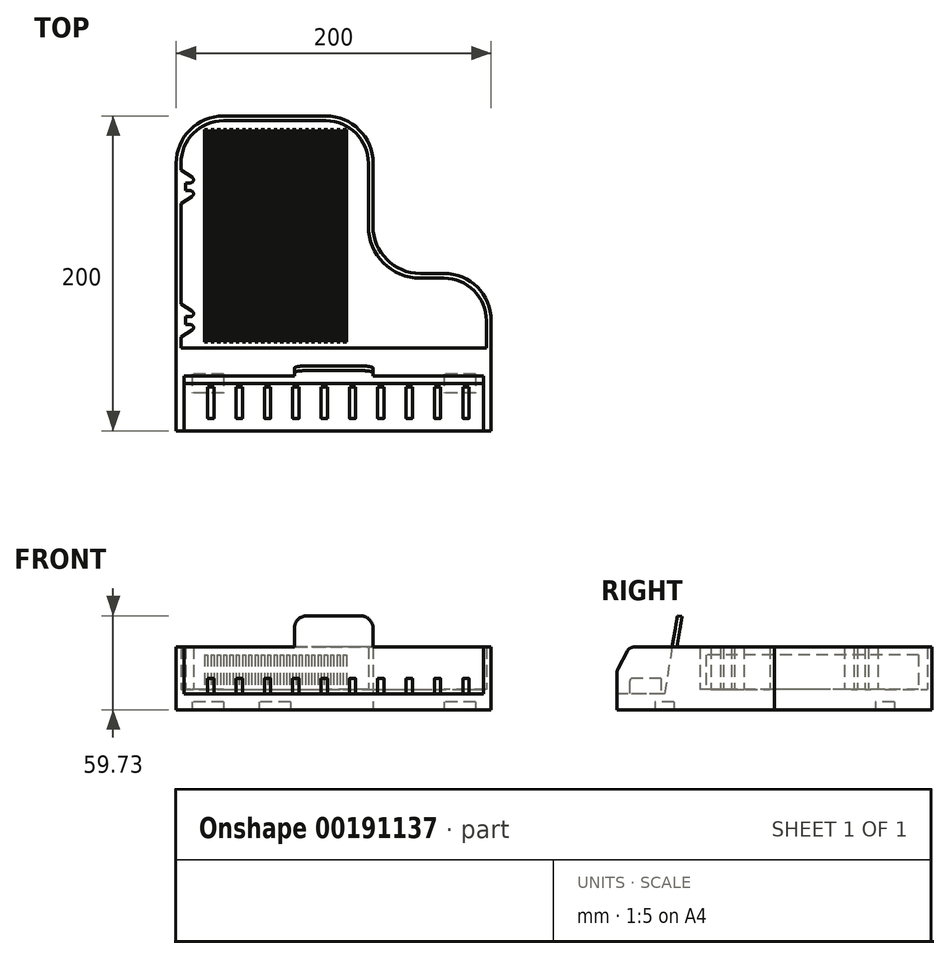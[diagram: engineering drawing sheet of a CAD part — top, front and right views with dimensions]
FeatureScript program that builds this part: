
annotation { "Feature Type Name" : "Feature", "Feature Type Description" : "" }
export const myFeature = defineFeature(function(context is Context, id is Id, definition is map)
    precondition{}
    {
        {
            var Q0;
            Q0=qCreatedBy(makeId("Top.planeOp"),FACE);
            var sketch = newSketch(context, id + "F0", { "sketchPlane" : qUnion([Q0])});
            skLineSegment(sketch, "E0.bottom", {"start": v(-100, 0) * mm, "end": v(100, 0) * mm});
            skLineSegment(sketch, "E0.top", {"start": v(-100, 200) * mm, "end": v(100, 200) * mm});
            skLineSegment(sketch, "E0.left", {"start": v(-100, 0) * mm, "end": v(-100, 200) * mm});
            skLineSegment(sketch, "E0.right", {"start": v(100, 0) * mm, "end": v(100, 200) * mm});
            skLineSegment(sketch, "E1.bottom", {"start": v(100, 200) * mm, "end": v(25, 200) * mm});
            skLineSegment(sketch, "E1.top", {"start": v(100, 100) * mm, "end": v(25, 100) * mm});
            skLineSegment(sketch, "E1.left", {"start": v(100, 200) * mm, "end": v(100, 100) * mm});
            skLineSegment(sketch, "E1.right", {"start": v(25, 200) * mm, "end": v(25, 100) * mm});
            skLineSegment(sketch, "E2", {"start": v(55, 209.14) * mm, "end": v(55, 81.97) * mm, "construction": true});
            skLineSegment(sketch, "E3", {"start": v(4.66, 130) * mm, "end": v(121.8, 130) * mm, "construction": true});
            skCircle(sketch, "E4", {"center": v(55, 130) * mm, "radius": 30 * mm});
            skLineSegment(sketch, "E5", {"start": v(70, 61.15) * mm, "end": v(70, 183.56) * mm, "construction": true});
            skLineSegment(sketch, "E6", {"start": v(-42.75, 70) * mm, "end": v(158.67, 70) * mm, "construction": true});
            skCircle(sketch, "E7", {"center": v(70, 70) * mm, "radius": 30 * mm});
            skPoint(sketch, "E7.centerSnap0", {"position": v(57.96, 70) * mm});
            skLineSegment(sketch, "E8", {"start": v(-5, 217.17) * mm, "end": v(-5, 99.03) * mm, "construction": true});
            skLineSegment(sketch, "E9", {"start": v(-141.82, 170) * mm, "end": v(13.69, 170) * mm, "construction": true});
            skLineSegment(sketch, "E10", {"start": v(-70, 225.7) * mm, "end": v(-70, 105.3) * mm, "construction": true});
            skCircle(sketch, "E11", {"center": v(-70, 170) * mm, "radius": 30 * mm});
            skCircle(sketch, "E12", {"center": v(-5, 170) * mm, "radius": 30 * mm});
            skSolve(sketch);
        }
        {
            var Q0;
            {var subQ0=sQuery(id+"F0.wireOp",EDGE,"E7");var subQ1=makeQuery(id+"F0.imprint","INTERSECT",VERTEX,{"derivedFrom":[sQuery(id+"F0.wireOp",EDGE,"E0.right"),subQ0]});Q0=makeQuery(id+"F0.imprint","IMPRINT",FACE,{"disambiguationData":[TD([[makeQuery(id+"F0.imprint","IMPRINT",EDGE,{"disambiguationData":[TD([[subQ1,-1.0]])],"derivedFrom":subQ0}),1.0]])]});}
            var Q1;
            {var subQ0=sQuery(id+"F0.wireOp",EDGE,"E11");var subQ1=makeQuery(id+"F0.imprint","INTERSECT",VERTEX,{"derivedFrom":[sQuery(id+"F0.wireOp",EDGE,"E0.top"),subQ0]});Q1=makeQuery(id+"F0.imprint","IMPRINT",FACE,{"disambiguationData":[TD([[makeQuery(id+"F0.imprint","IMPRINT",EDGE,{"disambiguationData":[TD([[subQ1,-1.0]])],"derivedFrom":subQ0}),1.0]])]});}
            var Q2;
            {var subQ0=sQuery(id+"F0.wireOp",EDGE,"E12");var subQ1=makeQuery(id+"F0.imprint","INTERSECT",VERTEX,{"derivedFrom":[sQuery(id+"F0.wireOp",EDGE,"E0.top"),subQ0]});Q2=makeQuery(id+"F0.imprint","IMPRINT",FACE,{"disambiguationData":[TD([[makeQuery(id+"F0.imprint","IMPRINT",EDGE,{"disambiguationData":[TD([[subQ1,1.0]])],"derivedFrom":subQ0}),1.0]])]});}
            var Q3;
            {var subQ17=sQuery(id+"F0.wireOp",EDGE,"E0.bottom");Q3=makeQuery(id+"F0.imprint","IMPRINT",FACE,{"disambiguationData":[TD([[makeQuery(id+"F0.imprint","IMPRINT",EDGE,{"derivedFrom":subQ17}),1.0]])]});}
            var Q4;
            {var subQ0=sQuery(id+"F0.wireOp",EDGE,"E1.right");var subQ1=sQuery(id+"F0.wireOp",EDGE,"E1.top");var subQ2=makeQuery(id+"F0.imprint","INTERSECT",VERTEX,{"derivedFrom":[subQ1,subQ0]});Q4=makeQuery(id+"F0.imprint","IMPRINT",FACE,{"disambiguationData":[TD([[makeQuery(id+"F0.imprint","IMPRINT",EDGE,{"disambiguationData":[TD([[subQ2,1.0]])],"derivedFrom":subQ1}),-1.0]])]});}
            extrude(context, id + "F1", {"entities" : qUnion([Q0, Q1, Q2, Q3, Q4]), "depth" : 40 * mm});
        }
        {
            var Q0;
            Q0=qCreatedBy(makeId("Top.planeOp"),FACE);
            cPlane(context, id + "F2", {"entities" : qUnion([Q0]), "cplaneType" : CPlaneType.OFFSET, "offset" : 5 * mm, "width" : 150 * mm, "height" : 150 * mm});
        }
        {
            var Q0;
            Q0=qCreatedBy(id+"F2.planeOp",FACE);
            var sketch = newSketch(context, id + "F3", { "sketchPlane" : qUnion([Q0])});
            skArc(sketch, "E13", {"start": v(-70, 197) * mm, "mid": v(-89.1, 189.1) * mm, "end": v(-97, 170) * mm});
            skArc(sketch, "E14", {"start": v(22, 170) * mm, "mid": v(14.1, 189.1) * mm, "end": v(-5, 197) * mm});
            skArc(sketch, "E15", {"start": v(22, 130) * mm, "mid": v(31.67, 106.67) * mm, "end": v(55, 97) * mm});
            skArc(sketch, "E16", {"start": v(97, 70) * mm, "mid": v(89.1, 89.1) * mm, "end": v(70, 97) * mm});
            skLineSegment(sketch, "E17", {"start": v(55, 97) * mm, "end": v(70, 97) * mm});
            skLineSegment(sketch, "E18", {"start": v(-70, 197) * mm, "end": v(-5, 197) * mm});
            skLineSegment(sketch, "E19", {"start": v(22, 170) * mm, "end": v(22, 130) * mm});
            skLineSegment(sketch, "E20", {"start": v(-131.7, 52.53) * mm, "end": v(133.85, 52.53) * mm, "construction": true});
            skLineSegment(sketch, "E21", {"start": v(97, 70) * mm, "end": v(97, 52.53) * mm});
            skLineSegment(sketch, "E22", {"start": v(-97, 170) * mm, "end": v(-97, 52.53) * mm});
            skLineSegment(sketch, "E23", {"start": v(-97, 52.53) * mm, "end": v(97, 52.53) * mm});
            skSolve(sketch);
        }
        {
            var Q0;
            {var subQ0=sQuery(id+"F3.wireOp",EDGE,"E13");var subQ1=makeQuery(id+"F3.imprint","INTERSECT",VERTEX,{"derivedFrom":[subQ0,sQuery(id+"F3.wireOp",EDGE,"E18")]});Q0=makeQuery(id+"F3.imprint","IMPRINT",FACE,{"disambiguationData":[TD([[makeQuery(id+"F3.imprint","IMPRINT",EDGE,{"disambiguationData":[TD([[subQ1,-1.0]])],"derivedFrom":subQ0}),1.0]])]});}
            var Q1;
            {var subQ0=sQuery(id+"F3.wireOp",EDGE,"E14");var subQ1=makeQuery(id+"F3.imprint","INTERSECT",VERTEX,{"derivedFrom":[subQ0,sQuery(id+"F3.wireOp",EDGE,"E18")]});Q1=makeQuery(id+"F3.imprint","IMPRINT",FACE,{"disambiguationData":[TD([[makeQuery(id+"F3.imprint","IMPRINT",EDGE,{"disambiguationData":[TD([[subQ1,1.0]])],"derivedFrom":subQ0}),1.0]])]});}
            var Q2;
            {var subQ0=sQuery(id+"F3.wireOp",EDGE,"E16");var subQ1=makeQuery(id+"F3.imprint","INTERSECT",VERTEX,{"derivedFrom":[subQ0,sQuery(id+"F3.wireOp",EDGE,"E17")]});Q2=makeQuery(id+"F3.imprint","IMPRINT",FACE,{"disambiguationData":[TD([[makeQuery(id+"F3.imprint","IMPRINT",EDGE,{"disambiguationData":[TD([[subQ1,1.0]])],"derivedFrom":subQ0}),1.0]])]});}
            var Q3;
            {var subQ0=sQuery(id+"F3.wireOp",EDGE,"E17");Q3=makeQuery(id+"F3.imprint","IMPRINT",FACE,{"disambiguationData":[TD([[makeQuery(id+"F3.imprint","IMPRINT",EDGE,{"derivedFrom":subQ0}),-1.0]])]});}
            extrude(context, id + "F4", {"entities" : qUnion([Q0, Q1, Q2, Q3]), "operationType" : NewBodyOperationType.REMOVE, "depth" : 35.7 * mm, "hasSecondDirection" : true, "secondDirectionOppositeDirection" : false, "secondDirectionDepth" : 8 * mm});
        }
        {
            var Q0;
            Q0=qCreatedBy(makeId("Right.planeOp"),FACE);
            var sketch = newSketch(context, id + "F5", { "sketchPlane" : qUnion([Q0])});
            skLineSegment(sketch, "E24", {"start": v(0, 40) * mm, "end": v(35, 40) * mm});
            skLineSegment(sketch, "E25", {"start": v(35, 40) * mm, "end": v(30, 10) * mm});
            skLineSegment(sketch, "E26", {"start": v(30, 10) * mm, "end": v(0, 10) * mm});
            skLineSegment(sketch, "E27", {"start": v(0, 10) * mm, "end": v(0, 40) * mm});
            skSolve(sketch);
        }
        {
            var Q0;
            Q0 = qSketchRegion(id + "F5", true);
            extrude(context, id + "F6", {"entities" : qUnion([Q0]), "operationType" : NewBodyOperationType.REMOVE, "endBound" : BoundingType.SYMMETRIC, "oppositeDirection" : true, "depth" : 190 * mm});
        }
        {
            var Q0;
            Q0=makeQuery(id+"F1.opExtrude","CAP_FACE",FACE,{"disambiguationData":[OSD([sQuery(id+"F0.wireOp",EDGE,"E0.bottom"),sQuery(id+"F0.wireOp",EDGE,"E0.top"),sQuery(id+"F0.wireOp",EDGE,"E0.left"),sQuery(id+"F0.wireOp",EDGE,"E0.right"),sQuery(id+"F0.wireOp",EDGE,"E1.top"),sQuery(id+"F0.wireOp",EDGE,"E1.right"),sQuery(id+"F0.wireOp",EDGE,"E4"),sQuery(id+"F0.wireOp",EDGE,"E7"),sQuery(id+"F0.wireOp",EDGE,"E11"),sQuery(id+"F0.wireOp",EDGE,"E12")])],"isStart":true});
            var sketch = newSketch(context, id + "F7", { "sketchPlane" : qUnion([Q0])});
            skLineSegment(sketch, "E28", {"start": v(91.06, -170) * mm, "end": v(-146.06, -170) * mm, "construction": true});
            skLineSegment(sketch, "E29", {"start": v(132.2, -30) * mm, "end": v(-157.53, -30) * mm, "construction": true});
            skLineSegment(sketch, "E30", {"start": v(80, -126.3) * mm, "end": v(80, 24.1) * mm, "construction": true});
            skLineSegment(sketch, "E31", {"start": v(-37.5, -226.49) * mm, "end": v(-37.5, 33.36) * mm, "construction": true});
            skLineSegment(sketch, "E32", {"start": v(-80, -225.96) * mm, "end": v(-80, 32.57) * mm, "construction": true});
            skLineSegment(sketch, "E33.bottom", {"start": v(90, -36) * mm, "end": v(70, -36) * mm});
            skLineSegment(sketch, "E33.top", {"start": v(90, -24) * mm, "end": v(70, -24) * mm});
            skLineSegment(sketch, "E33.left", {"start": v(90, -36) * mm, "end": v(90, -24) * mm});
            skLineSegment(sketch, "E33.right", {"start": v(70, -36) * mm, "end": v(70, -24) * mm});
            skLineSegment(sketch, "E34.bottom", {"start": v(-70, -36) * mm, "end": v(-90, -36) * mm});
            skLineSegment(sketch, "E34.top", {"start": v(-70, -24) * mm, "end": v(-90, -24) * mm});
            skLineSegment(sketch, "E34.left", {"start": v(-70, -36) * mm, "end": v(-70, -24) * mm});
            skLineSegment(sketch, "E34.right", {"start": v(-90, -36) * mm, "end": v(-90, -24) * mm});
            skPoint(sketch, "E35.firstSnap0", {"position": v(-27.5, -170) * mm});
            skLineSegment(sketch, "E35.bottom", {"start": v(-27.5, -176) * mm, "end": v(-47.5, -176) * mm});
            skLineSegment(sketch, "E35.top", {"start": v(-27.5, -164) * mm, "end": v(-47.5, -164) * mm});
            skLineSegment(sketch, "E35.left", {"start": v(-27.5, -176) * mm, "end": v(-27.5, -164) * mm});
            skLineSegment(sketch, "E35.right", {"start": v(-47.5, -176) * mm, "end": v(-47.5, -164) * mm});
            skSolve(sketch);
        }
        {
            var Q0;
            Q0 = qSketchRegion(id + "F7", true);
            extrude(context, id + "F8", {"entities" : qUnion([Q0]), "operationType" : NewBodyOperationType.REMOVE, "oppositeDirection" : true, "depth" : 5 * mm});
        }
        {
            var Q0;
            {var subQ0=sQuery(id+"F0.wireOp",EDGE,"E0.bottom");var subQ1=sQuery(id+"F0.wireOp",EDGE,"E0.left");Q0=makeQuery(id+"F6.boolean.opBoolean","SPLIT",EDGE,{"disambiguationData":[TD([makeQuery(id+"F1.opExtrude","SWEPT_FACE",FACE,{"disambiguationData":[OSD([subQ1])]})])],"derivedFrom":makeQuery(id+"F1.opExtrude","CAP_EDGE",EDGE,{"disambiguationData":[OSD([subQ0])],"isStart":false})});}
            var Q1;
            {var subQ0=sQuery(id+"F0.wireOp",EDGE,"E0.bottom");var subQ1=sQuery(id+"F0.wireOp",EDGE,"E0.right");Q1=makeQuery(id+"F6.boolean.opBoolean","SPLIT",EDGE,{"disambiguationData":[TD([makeQuery(id+"F1.opExtrude","SWEPT_FACE",FACE,{"disambiguationData":[OSD([subQ1])]})])],"derivedFrom":makeQuery(id+"F1.opExtrude","CAP_EDGE",EDGE,{"disambiguationData":[OSD([subQ0])],"isStart":false})});}
            chamfer(context, id + "F9", {"entities" : qUnion([Q0, Q1]), "chamferType" : ChamferType.TWO_OFFSETS, "width1" : 8 * mm, "oppositeDirection" : false, "width2" : 15 * mm, "tangentPropagation" : true});
        }
        {
            var Q0;
            {var subQ0=sQuery(id+"F0.wireOp",EDGE,"E0.right");var subQ1=sQuery(id+"F0.wireOp",EDGE,"E0.bottom");var subQ2=makeQuery(id+"F1.opExtrude","CAP_FACE",FACE,{"disambiguationData":[OSD([subQ1,sQuery(id+"F0.wireOp",EDGE,"E0.top"),sQuery(id+"F0.wireOp",EDGE,"E0.left"),subQ0,sQuery(id+"F0.wireOp",EDGE,"E1.top"),sQuery(id+"F0.wireOp",EDGE,"E1.right"),sQuery(id+"F0.wireOp",EDGE,"E4"),sQuery(id+"F0.wireOp",EDGE,"E7"),sQuery(id+"F0.wireOp",EDGE,"E11"),sQuery(id+"F0.wireOp",EDGE,"E12")])],"isStart":false});Q0=makeQuery(id+"F9.opChamfer","BLEND_EDGE",EDGE,{"blendedFrom":[makeQuery(id+"F6.boolean.opBoolean","SPLIT",EDGE,{"disambiguationData":[TD([makeQuery(id+"F1.opExtrude","SWEPT_FACE",FACE,{"disambiguationData":[OSD([subQ0])]})])],"derivedFrom":makeQuery(id+"F1.opExtrude","CAP_EDGE",EDGE,{"disambiguationData":[OSD([subQ1])],"isStart":false})}),subQ2],"blendedInto":[subQ2]});}
            var Q1;
            {var subQ0=sQuery(id+"F0.wireOp",EDGE,"E0.bottom");var subQ1=makeQuery(id+"F1.opExtrude","SWEPT_FACE",FACE,{"disambiguationData":[OSD([subQ0])]});var subQ2=sQuery(id+"F0.wireOp",EDGE,"E0.right");Q1=makeQuery(id+"F9.opChamfer","BLEND_EDGE",EDGE,{"blendedFrom":[makeQuery(id+"F6.boolean.opBoolean","SPLIT",EDGE,{"disambiguationData":[TD([makeQuery(id+"F1.opExtrude","SWEPT_FACE",FACE,{"disambiguationData":[OSD([subQ2])]})])],"derivedFrom":makeQuery(id+"F1.opExtrude","CAP_EDGE",EDGE,{"disambiguationData":[OSD([subQ0])],"isStart":false})}),subQ1],"blendedInto":[subQ1]});}
            var Q2;
            {var subQ0=sQuery(id+"F0.wireOp",EDGE,"E0.bottom");var subQ1=makeQuery(id+"F1.opExtrude","SWEPT_FACE",FACE,{"disambiguationData":[OSD([subQ0])]});var subQ2=sQuery(id+"F0.wireOp",EDGE,"E0.left");Q2=makeQuery(id+"F9.opChamfer","BLEND_EDGE",EDGE,{"blendedFrom":[makeQuery(id+"F6.boolean.opBoolean","SPLIT",EDGE,{"disambiguationData":[TD([makeQuery(id+"F1.opExtrude","SWEPT_FACE",FACE,{"disambiguationData":[OSD([subQ2])]})])],"derivedFrom":makeQuery(id+"F1.opExtrude","CAP_EDGE",EDGE,{"disambiguationData":[OSD([subQ0])],"isStart":false})}),subQ1],"blendedInto":[subQ1]});}
            var Q3;
            {var subQ0=sQuery(id+"F0.wireOp",EDGE,"E0.left");var subQ1=sQuery(id+"F0.wireOp",EDGE,"E0.bottom");var subQ2=makeQuery(id+"F1.opExtrude","CAP_FACE",FACE,{"disambiguationData":[OSD([subQ1,sQuery(id+"F0.wireOp",EDGE,"E0.top"),subQ0,sQuery(id+"F0.wireOp",EDGE,"E0.right"),sQuery(id+"F0.wireOp",EDGE,"E1.top"),sQuery(id+"F0.wireOp",EDGE,"E1.right"),sQuery(id+"F0.wireOp",EDGE,"E4"),sQuery(id+"F0.wireOp",EDGE,"E7"),sQuery(id+"F0.wireOp",EDGE,"E11"),sQuery(id+"F0.wireOp",EDGE,"E12")])],"isStart":false});Q3=makeQuery(id+"F9.opChamfer","BLEND_EDGE",EDGE,{"blendedFrom":[makeQuery(id+"F6.boolean.opBoolean","SPLIT",EDGE,{"disambiguationData":[TD([makeQuery(id+"F1.opExtrude","SWEPT_FACE",FACE,{"disambiguationData":[OSD([subQ0])]})])],"derivedFrom":makeQuery(id+"F1.opExtrude","CAP_EDGE",EDGE,{"disambiguationData":[OSD([subQ1])],"isStart":false})}),subQ2],"blendedInto":[subQ2]});}
            fillet(context, id + "F10", {"entities" : qUnion([Q0, Q1, Q2, Q3]), "radius" : 5 * mm, "tangentPropagation" : true, "allowEdgeOverflow" : false});
        }
        {
            var Q0;
            Q0=makeQuery(id+"F6.boolean.opBoolean","COPY",FACE,{"derivedFrom":makeQuery(id+"F6.opExtrude","SWEPT_FACE",FACE,{"disambiguationData":[OSD([sQuery(id+"F5.wireOp",EDGE,"E26")])]})});
            var sketch = newSketch(context, id + "F11", { "sketchPlane" : qUnion([Q0])});
            skLineSegment(sketch, "E36.bottom", {"start": v(-80, 28) * mm, "end": v(-76, 28) * mm});
            skLineSegment(sketch, "E36.top", {"start": v(-80, 8) * mm, "end": v(-76, 8) * mm});
            skLineSegment(sketch, "E36.left", {"start": v(-80, 28) * mm, "end": v(-80, 8) * mm});
            skLineSegment(sketch, "E36.right", {"start": v(-76, 28) * mm, "end": v(-76, 8) * mm});
            skLineSegment(sketch, "E37.1.0.0", {"start": v(-62, 28) * mm, "end": v(-62, 8) * mm});
            skLineSegment(sketch, "E37.1.0.1", {"start": v(-62, 28) * mm, "end": v(-58, 28) * mm});
            skLineSegment(sketch, "E37.1.0.2", {"start": v(-58, 28) * mm, "end": v(-58, 8) * mm});
            skLineSegment(sketch, "E37.1.0.3", {"start": v(-62, 8) * mm, "end": v(-58, 8) * mm});
            skLineSegment(sketch, "E37.2.0.0", {"start": v(-44, 28) * mm, "end": v(-44, 8) * mm});
            skLineSegment(sketch, "E37.2.0.1", {"start": v(-44, 28) * mm, "end": v(-40, 28) * mm});
            skLineSegment(sketch, "E37.2.0.2", {"start": v(-40, 28) * mm, "end": v(-40, 8) * mm});
            skLineSegment(sketch, "E37.2.0.3", {"start": v(-44, 8) * mm, "end": v(-40, 8) * mm});
            skLineSegment(sketch, "E37.3.0.0", {"start": v(-26, 28) * mm, "end": v(-26, 8) * mm});
            skLineSegment(sketch, "E37.3.0.1", {"start": v(-26, 28) * mm, "end": v(-22, 28) * mm});
            skLineSegment(sketch, "E37.3.0.2", {"start": v(-22, 28) * mm, "end": v(-22, 8) * mm});
            skLineSegment(sketch, "E37.3.0.3", {"start": v(-26, 8) * mm, "end": v(-22, 8) * mm});
            skLineSegment(sketch, "E37.4.0.0", {"start": v(-8, 28) * mm, "end": v(-8, 8) * mm});
            skLineSegment(sketch, "E37.4.0.1", {"start": v(-8, 28) * mm, "end": v(-4, 28) * mm});
            skLineSegment(sketch, "E37.4.0.2", {"start": v(-4, 28) * mm, "end": v(-4, 8) * mm});
            skLineSegment(sketch, "E37.4.0.3", {"start": v(-8, 8) * mm, "end": v(-4, 8) * mm});
            skLineSegment(sketch, "E37.5.0.0", {"start": v(10, 28) * mm, "end": v(10, 8) * mm});
            skLineSegment(sketch, "E37.5.0.1", {"start": v(10, 28) * mm, "end": v(14, 28) * mm});
            skLineSegment(sketch, "E37.5.0.2", {"start": v(14, 28) * mm, "end": v(14, 8) * mm});
            skLineSegment(sketch, "E37.5.0.3", {"start": v(10, 8) * mm, "end": v(14, 8) * mm});
            skLineSegment(sketch, "E37.6.0.0", {"start": v(28, 28) * mm, "end": v(28, 8) * mm});
            skLineSegment(sketch, "E37.6.0.1", {"start": v(28, 28) * mm, "end": v(32, 28) * mm});
            skLineSegment(sketch, "E37.6.0.2", {"start": v(32, 28) * mm, "end": v(32, 8) * mm});
            skLineSegment(sketch, "E37.6.0.3", {"start": v(28, 8) * mm, "end": v(32, 8) * mm});
            skLineSegment(sketch, "E37.direction1", {"start": v(-80, 8) * mm, "end": v(-62, 8) * mm, "construction": true});
            skLineSegment(sketch, "E38.0.7.0", {"start": v(46, 28) * mm, "end": v(46, 8) * mm});
            skLineSegment(sketch, "E38.3.7.0", {"start": v(46, 28) * mm, "end": v(50, 28) * mm});
            skLineSegment(sketch, "E38.6.7.0", {"start": v(50, 28) * mm, "end": v(50, 8) * mm});
            skLineSegment(sketch, "E38.9.7.0", {"start": v(46, 8) * mm, "end": v(50, 8) * mm});
            skLineSegment(sketch, "E38.0.8.0", {"start": v(64, 28) * mm, "end": v(64, 8) * mm});
            skLineSegment(sketch, "E38.3.8.0", {"start": v(64, 28) * mm, "end": v(68, 28) * mm});
            skLineSegment(sketch, "E38.6.8.0", {"start": v(68, 28) * mm, "end": v(68, 8) * mm});
            skLineSegment(sketch, "E38.9.8.0", {"start": v(64, 8) * mm, "end": v(68, 8) * mm});
            skLineSegment(sketch, "E39.0.9.0", {"start": v(82, 28) * mm, "end": v(82, 8) * mm});
            skLineSegment(sketch, "E39.3.9.0", {"start": v(82, 28) * mm, "end": v(86, 28) * mm});
            skLineSegment(sketch, "E39.6.9.0", {"start": v(86, 28) * mm, "end": v(86, 8) * mm});
            skLineSegment(sketch, "E39.9.9.0", {"start": v(82, 8) * mm, "end": v(86, 8) * mm});
            skSolve(sketch);
        }
        {
            var Q0;
            Q0 = qSketchRegion(id + "F11", true);
            extrude(context, id + "F12", {"entities" : qUnion([Q0]), "operationType" : NewBodyOperationType.ADD, "depth" : 10 * mm});
        }
        {
            var Q0;
            Q0=makeQuery(id+"F12.opExtrude","CAP_EDGE",EDGE,{"disambiguationData":[OSD([sQuery(id+"F11.wireOp",EDGE,"E36.top")])],"isStart":false});
            var Q1;
            Q1=makeQuery(id+"F12.opExtrude","CAP_EDGE",EDGE,{"disambiguationData":[OSD([sQuery(id+"F11.wireOp",EDGE,"E37.1.0.3")])],"isStart":false});
            var Q2;
            Q2=makeQuery(id+"F12.opExtrude","CAP_EDGE",EDGE,{"disambiguationData":[OSD([sQuery(id+"F11.wireOp",EDGE,"E37.2.0.3")])],"isStart":false});
            var Q3;
            Q3=makeQuery(id+"F12.opExtrude","CAP_EDGE",EDGE,{"disambiguationData":[OSD([sQuery(id+"F11.wireOp",EDGE,"E37.3.0.3")])],"isStart":false});
            var Q4;
            Q4=makeQuery(id+"F12.opExtrude","CAP_EDGE",EDGE,{"disambiguationData":[OSD([sQuery(id+"F11.wireOp",EDGE,"E37.4.0.3")])],"isStart":false});
            var Q5;
            Q5=makeQuery(id+"F12.opExtrude","CAP_EDGE",EDGE,{"disambiguationData":[OSD([sQuery(id+"F11.wireOp",EDGE,"E37.5.0.3")])],"isStart":false});
            var Q6;
            Q6=makeQuery(id+"F12.opExtrude","CAP_EDGE",EDGE,{"disambiguationData":[OSD([sQuery(id+"F11.wireOp",EDGE,"E37.6.0.3")])],"isStart":false});
            var Q7;
            Q7=makeQuery(id+"F12.opExtrude","CAP_EDGE",EDGE,{"disambiguationData":[OSD([sQuery(id+"F11.wireOp",EDGE,"E38.9.7.0")])],"isStart":false});
            var Q8;
            Q8=makeQuery(id+"F12.opExtrude","CAP_EDGE",EDGE,{"disambiguationData":[OSD([sQuery(id+"F11.wireOp",EDGE,"E38.9.8.0")])],"isStart":false});
            var Q9;
            Q9=makeQuery(id+"F12.opExtrude","CAP_EDGE",EDGE,{"disambiguationData":[OSD([sQuery(id+"F11.wireOp",EDGE,"E39.9.9.0")])],"isStart":false});
            fillet(context, id + "F13", {"entities" : qUnion([Q0, Q1, Q2, Q3, Q4, Q5, Q6, Q7, Q8, Q9]), "radius" : 2 * mm, "tangentPropagation" : true, "allowEdgeOverflow" : false});
        }
        {
            var Q0;
            Q0=makeQuery(id+"FI102JTuiumcnOo_1.boolean.opBoolean","MERGE",FACE,{"derivedFrom":[makeQuery(id+"F6.boolean.opBoolean","COPY",FACE,{"derivedFrom":makeQuery(id+"F6.opExtrude","SWEPT_FACE",FACE,{"disambiguationData":[OSD([sQuery(id+"F5.wireOp",EDGE,"E25")])]})}),makeQuery(id+"FI102JTuiumcnOo_1.opExtrude","SWEPT_FACE",FACE,{"disambiguationData":[OSD([sQuery(id+"FAZ91UPh5DJX8Yx_1.wireOp",EDGE,"L1Z9kh2t-6Zbd-3Afq-hM0M-9ZzipnV0yRQ6")])]})]});
            var sketch = newSketch(context, id + "F14", { "sketchPlane" : qUnion([Q0])});
            skLineSegment(sketch, "E40.bottom", {"start": v(-25, 45.2) * mm, "end": v(-5, 45.2) * mm});
            skLineSegment(sketch, "E40.top", {"start": v(-25, 65.2) * mm, "end": v(-5, 65.2) * mm});
            skLineSegment(sketch, "E40.left", {"start": v(-25, 45.2) * mm, "end": v(-25, 65.2) * mm});
            skLineSegment(sketch, "E40.right", {"start": v(-5, 45.2) * mm, "end": v(-5, 65.2) * mm});
            skLineSegment(sketch, "E41.bottom", {"start": v(-5, 45.2) * mm, "end": v(25, 45.2) * mm});
            skLineSegment(sketch, "E41.top", {"start": v(-5, 65.2) * mm, "end": v(25, 65.2) * mm});
            skLineSegment(sketch, "E41.right", {"start": v(25, 45.2) * mm, "end": v(25, 65.2) * mm});
            skSolve(sketch);
        }
        {
            var Q0;
            Q0 = qSketchRegion(id + "F14", true);
            extrude(context, id + "F15", {"entities" : qUnion([Q0]), "operationType" : NewBodyOperationType.ADD, "oppositeDirection" : true, "depth" : 3 * mm});
        }
        {
            var Q0;
            Q0=makeQuery(id+"F15.opExtrude","SWEPT_EDGE",EDGE,{"disambiguationData":[OSD([sQuery(id+"F14.wireOp",EDGE,"E40.top"),sQuery(id+"F14.wireOp",EDGE,"E40.left")])]});
            var Q1;
            Q1=makeQuery(id+"F15.opExtrude","SWEPT_EDGE",EDGE,{"disambiguationData":[OSD([sQuery(id+"F14.wireOp",EDGE,"E41.top"),sQuery(id+"F14.wireOp",EDGE,"E41.right")])]});
            fillet(context, id + "F16", {"entities" : qUnion([Q0, Q1]), "radius" : 8 * mm, "tangentPropagation" : true, "allowEdgeOverflow" : false});
        }
        {
            var Q0;
            Q0=makeQuery(id+"F4.boolean.opBoolean","COPY",FACE,{"derivedFrom":makeQuery(id+"F4.opExtrude","CAP_FACE",FACE,{"disambiguationData":[OSD([sQuery(id+"F3.wireOp",EDGE,"E13"),sQuery(id+"F3.wireOp",EDGE,"E14"),sQuery(id+"F3.wireOp",EDGE,"E15"),sQuery(id+"F3.wireOp",EDGE,"E16"),sQuery(id+"F3.wireOp",EDGE,"E17"),sQuery(id+"F3.wireOp",EDGE,"E18"),sQuery(id+"F3.wireOp",EDGE,"E19"),sQuery(id+"F3.wireOp",EDGE,"E21"),sQuery(id+"F3.wireOp",EDGE,"E22"),sQuery(id+"F3.wireOp",EDGE,"E23")])],"isStart":true})});
            var sketch = newSketch(context, id + "F17", { "sketchPlane" : qUnion([Q0])});
            skLineSegment(sketch, "E42", {"start": v(-97, 165.53) * mm, "end": v(-89, 160.53) * mm});
            skLineSegment(sketch, "E43", {"start": v(-89, 160.53) * mm, "end": v(-89, 157.53) * mm});
            skLineSegment(sketch, "E44", {"start": v(-89, 157.53) * mm, "end": v(-94, 157.53) * mm});
            skLineSegment(sketch, "E45", {"start": v(-94, 157.53) * mm, "end": v(-94, 152.53) * mm});
            skLineSegment(sketch, "E46", {"start": v(-94, 152.53) * mm, "end": v(-89, 152.53) * mm});
            skLineSegment(sketch, "E47", {"start": v(-89, 152.53) * mm, "end": v(-89, 149.53) * mm});
            skLineSegment(sketch, "E48", {"start": v(-89, 149.53) * mm, "end": v(-97, 144.53) * mm});
            skLineSegment(sketch, "E49", {"start": v(-97, 144.53) * mm, "end": v(-97, 165.53) * mm});
            skLineSegment(sketch, "E50", {"start": v(-145.72, 112.53) * mm, "end": v(15.07, 112.53) * mm, "construction": true});
            skLineSegment(sketch, "E51.MirrorCS", {"start": v(-89, 67.53) * mm, "end": v(-94, 67.53) * mm});
            skLineSegment(sketch, "E52.MirrorCS", {"start": v(-89, 64.53) * mm, "end": v(-89, 67.53) * mm});
            skLineSegment(sketch, "E53.MirrorCS", {"start": v(-94, 67.53) * mm, "end": v(-94, 72.53) * mm});
            skLineSegment(sketch, "E54.MirrorCS", {"start": v(-94, 72.53) * mm, "end": v(-89, 72.53) * mm});
            skLineSegment(sketch, "E55.MirrorCS", {"start": v(-89, 72.53) * mm, "end": v(-89, 75.53) * mm});
            skLineSegment(sketch, "E56.MirrorCS", {"start": v(-89, 75.53) * mm, "end": v(-97, 80.53) * mm});
            skLineSegment(sketch, "E57.MirrorCS", {"start": v(-97, 59.53) * mm, "end": v(-89, 64.53) * mm});
            skLineSegment(sketch, "E58.MirrorCS", {"start": v(-97, 80.53) * mm, "end": v(-97, 59.53) * mm});
            skSolve(sketch);
        }
        {
            var Q0;
            Q0 = qSketchRegion(id + "F17", true);
            extrude(context, id + "F18", {"entities" : qUnion([Q0]), "operationType" : NewBodyOperationType.ADD, "depth" : 27 * mm});
        }
        {
            var Q0;
            Q0=makeQuery(id+"F18.opExtrude","SWEPT_EDGE",EDGE,{"disambiguationData":[OSD([sQuery(id+"F17.wireOp",EDGE,"E52.MirrorCS"),sQuery(id+"F17.wireOp",EDGE,"E57.MirrorCS")])]});
            var Q1;
            Q1=makeQuery(id+"F18.opExtrude","SWEPT_EDGE",EDGE,{"disambiguationData":[OSD([sQuery(id+"F17.wireOp",EDGE,"E54.MirrorCS"),sQuery(id+"F17.wireOp",EDGE,"E55.MirrorCS")])]});
            var Q2;
            Q2=makeQuery(id+"F18.opExtrude","SWEPT_EDGE",EDGE,{"disambiguationData":[OSD([sQuery(id+"F17.wireOp",EDGE,"E51.MirrorCS"),sQuery(id+"F17.wireOp",EDGE,"E52.MirrorCS")])]});
            var Q3;
            Q3=makeQuery(id+"F18.opExtrude","SWEPT_EDGE",EDGE,{"disambiguationData":[OSD([sQuery(id+"F17.wireOp",EDGE,"E55.MirrorCS"),sQuery(id+"F17.wireOp",EDGE,"E56.MirrorCS")])]});
            var Q4;
            Q4=makeQuery(id+"F18.opExtrude","SWEPT_EDGE",EDGE,{"disambiguationData":[OSD([sQuery(id+"F17.wireOp",EDGE,"E47"),sQuery(id+"F17.wireOp",EDGE,"E48")])]});
            var Q5;
            Q5=makeQuery(id+"F18.opExtrude","SWEPT_EDGE",EDGE,{"disambiguationData":[OSD([sQuery(id+"F17.wireOp",EDGE,"E46"),sQuery(id+"F17.wireOp",EDGE,"E47")])]});
            var Q6;
            Q6=makeQuery(id+"F18.opExtrude","SWEPT_EDGE",EDGE,{"disambiguationData":[OSD([sQuery(id+"F17.wireOp",EDGE,"E43"),sQuery(id+"F17.wireOp",EDGE,"E44")])]});
            var Q7;
            Q7=makeQuery(id+"F18.opExtrude","SWEPT_EDGE",EDGE,{"disambiguationData":[OSD([sQuery(id+"F17.wireOp",EDGE,"E42"),sQuery(id+"F17.wireOp",EDGE,"E43")])]});
            fillet(context, id + "F19", {"entities" : qUnion([Q0, Q1, Q2, Q3, Q4, Q5, Q6, Q7]), "radius" : 2 * mm, "tangentPropagation" : true, "allowEdgeOverflow" : false});
        }
        {
            var Q0;
            Q0=makeQuery(id+"F4.boolean.opBoolean","COPY",FACE,{"derivedFrom":makeQuery(id+"F4.opExtrude","CAP_FACE",FACE,{"disambiguationData":[OSD([sQuery(id+"F3.wireOp",EDGE,"E13"),sQuery(id+"F3.wireOp",EDGE,"E14"),sQuery(id+"F3.wireOp",EDGE,"E15"),sQuery(id+"F3.wireOp",EDGE,"E16"),sQuery(id+"F3.wireOp",EDGE,"E17"),sQuery(id+"F3.wireOp",EDGE,"E18"),sQuery(id+"F3.wireOp",EDGE,"E19"),sQuery(id+"F3.wireOp",EDGE,"E21"),sQuery(id+"F3.wireOp",EDGE,"E22"),sQuery(id+"F3.wireOp",EDGE,"E23")])],"isStart":true})});
            var sketch = newSketch(context, id + "F20", { "sketchPlane" : qUnion([Q0])});
            skLineSegment(sketch, "E59.bottom", {"start": v(-82, 191.53) * mm, "end": v(-80, 191.53) * mm});
            skLineSegment(sketch, "E59.top", {"start": v(-82, 56.53) * mm, "end": v(-80, 56.53) * mm});
            skLineSegment(sketch, "E59.left", {"start": v(-82, 191.53) * mm, "end": v(-82, 56.53) * mm});
            skLineSegment(sketch, "E59.right", {"start": v(-80, 191.53) * mm, "end": v(-80, 56.53) * mm});
            skLineSegment(sketch, "E60.1.0.0", {"start": v(-78, 191.53) * mm, "end": v(-78, 56.53) * mm});
            skLineSegment(sketch, "E60.1.0.1", {"start": v(-78, 191.53) * mm, "end": v(-76, 191.53) * mm});
            skLineSegment(sketch, "E60.1.0.2", {"start": v(-76, 191.53) * mm, "end": v(-76, 56.53) * mm});
            skLineSegment(sketch, "E60.1.0.3", {"start": v(-78, 56.53) * mm, "end": v(-76, 56.53) * mm});
            skLineSegment(sketch, "E60.2.0.0", {"start": v(-74, 191.53) * mm, "end": v(-74, 56.53) * mm});
            skLineSegment(sketch, "E60.2.0.1", {"start": v(-74, 191.53) * mm, "end": v(-72, 191.53) * mm});
            skLineSegment(sketch, "E60.2.0.2", {"start": v(-72, 191.53) * mm, "end": v(-72, 56.53) * mm});
            skLineSegment(sketch, "E60.2.0.3", {"start": v(-74, 56.53) * mm, "end": v(-72, 56.53) * mm});
            skLineSegment(sketch, "E60.3.0.0", {"start": v(-70, 191.53) * mm, "end": v(-70, 56.53) * mm});
            skLineSegment(sketch, "E60.3.0.1", {"start": v(-70, 191.53) * mm, "end": v(-68, 191.53) * mm});
            skLineSegment(sketch, "E60.3.0.2", {"start": v(-68, 191.53) * mm, "end": v(-68, 56.53) * mm});
            skLineSegment(sketch, "E60.3.0.3", {"start": v(-70, 56.53) * mm, "end": v(-68, 56.53) * mm});
            skLineSegment(sketch, "E60.4.0.0", {"start": v(-66, 191.53) * mm, "end": v(-66, 56.53) * mm});
            skLineSegment(sketch, "E60.4.0.1", {"start": v(-66, 191.53) * mm, "end": v(-64, 191.53) * mm});
            skLineSegment(sketch, "E60.4.0.2", {"start": v(-64, 191.53) * mm, "end": v(-64, 56.53) * mm});
            skLineSegment(sketch, "E60.4.0.3", {"start": v(-66, 56.53) * mm, "end": v(-64, 56.53) * mm});
            skLineSegment(sketch, "E60.5.0.0", {"start": v(-62, 191.53) * mm, "end": v(-62, 56.53) * mm});
            skLineSegment(sketch, "E60.5.0.1", {"start": v(-62, 191.53) * mm, "end": v(-60, 191.53) * mm});
            skLineSegment(sketch, "E60.5.0.2", {"start": v(-60, 191.53) * mm, "end": v(-60, 56.53) * mm});
            skLineSegment(sketch, "E60.5.0.3", {"start": v(-62, 56.53) * mm, "end": v(-60, 56.53) * mm});
            skLineSegment(sketch, "E60.6.0.0", {"start": v(-58, 191.53) * mm, "end": v(-58, 56.53) * mm});
            skLineSegment(sketch, "E60.6.0.1", {"start": v(-58, 191.53) * mm, "end": v(-56, 191.53) * mm});
            skLineSegment(sketch, "E60.6.0.2", {"start": v(-56, 191.53) * mm, "end": v(-56, 56.53) * mm});
            skLineSegment(sketch, "E60.6.0.3", {"start": v(-58, 56.53) * mm, "end": v(-56, 56.53) * mm});
            skLineSegment(sketch, "E60.7.0.0", {"start": v(-54, 191.53) * mm, "end": v(-54, 56.53) * mm});
            skLineSegment(sketch, "E60.7.0.1", {"start": v(-54, 191.53) * mm, "end": v(-52, 191.53) * mm});
            skLineSegment(sketch, "E60.7.0.2", {"start": v(-52, 191.53) * mm, "end": v(-52, 56.53) * mm});
            skLineSegment(sketch, "E60.7.0.3", {"start": v(-54, 56.53) * mm, "end": v(-52, 56.53) * mm});
            skLineSegment(sketch, "E60.8.0.0", {"start": v(-50, 191.53) * mm, "end": v(-50, 56.53) * mm});
            skLineSegment(sketch, "E60.8.0.1", {"start": v(-50, 191.53) * mm, "end": v(-48, 191.53) * mm});
            skLineSegment(sketch, "E60.8.0.2", {"start": v(-48, 191.53) * mm, "end": v(-48, 56.53) * mm});
            skLineSegment(sketch, "E60.8.0.3", {"start": v(-50, 56.53) * mm, "end": v(-48, 56.53) * mm});
            skLineSegment(sketch, "E60.9.0.0", {"start": v(-46, 191.53) * mm, "end": v(-46, 56.53) * mm});
            skLineSegment(sketch, "E60.9.0.1", {"start": v(-46, 191.53) * mm, "end": v(-44, 191.53) * mm});
            skLineSegment(sketch, "E60.9.0.2", {"start": v(-44, 191.53) * mm, "end": v(-44, 56.53) * mm});
            skLineSegment(sketch, "E60.9.0.3", {"start": v(-46, 56.53) * mm, "end": v(-44, 56.53) * mm});
            skLineSegment(sketch, "E60.10.0.0", {"start": v(-42, 191.53) * mm, "end": v(-42, 56.53) * mm});
            skLineSegment(sketch, "E60.10.0.1", {"start": v(-42, 191.53) * mm, "end": v(-40, 191.53) * mm});
            skLineSegment(sketch, "E60.10.0.2", {"start": v(-40, 191.53) * mm, "end": v(-40, 56.53) * mm});
            skLineSegment(sketch, "E60.10.0.3", {"start": v(-42, 56.53) * mm, "end": v(-40, 56.53) * mm});
            skLineSegment(sketch, "E60.11.0.0", {"start": v(-38, 191.53) * mm, "end": v(-38, 56.53) * mm});
            skLineSegment(sketch, "E60.11.0.1", {"start": v(-38, 191.53) * mm, "end": v(-36, 191.53) * mm});
            skLineSegment(sketch, "E60.11.0.2", {"start": v(-36, 191.53) * mm, "end": v(-36, 56.53) * mm});
            skLineSegment(sketch, "E60.11.0.3", {"start": v(-38, 56.53) * mm, "end": v(-36, 56.53) * mm});
            skLineSegment(sketch, "E60.12.0.0", {"start": v(-34, 191.53) * mm, "end": v(-34, 56.53) * mm});
            skLineSegment(sketch, "E60.12.0.1", {"start": v(-34, 191.53) * mm, "end": v(-32, 191.53) * mm});
            skLineSegment(sketch, "E60.12.0.2", {"start": v(-32, 191.53) * mm, "end": v(-32, 56.53) * mm});
            skLineSegment(sketch, "E60.12.0.3", {"start": v(-34, 56.53) * mm, "end": v(-32, 56.53) * mm});
            skLineSegment(sketch, "E60.13.0.0", {"start": v(-30, 191.53) * mm, "end": v(-30, 56.53) * mm});
            skLineSegment(sketch, "E60.13.0.1", {"start": v(-30, 191.53) * mm, "end": v(-28, 191.53) * mm});
            skLineSegment(sketch, "E60.13.0.2", {"start": v(-28, 191.53) * mm, "end": v(-28, 56.53) * mm});
            skLineSegment(sketch, "E60.13.0.3", {"start": v(-30, 56.53) * mm, "end": v(-28, 56.53) * mm});
            skLineSegment(sketch, "E60.14.0.0", {"start": v(-26, 191.53) * mm, "end": v(-26, 56.53) * mm});
            skLineSegment(sketch, "E60.14.0.1", {"start": v(-26, 191.53) * mm, "end": v(-24, 191.53) * mm});
            skLineSegment(sketch, "E60.14.0.2", {"start": v(-24, 191.53) * mm, "end": v(-24, 56.53) * mm});
            skLineSegment(sketch, "E60.14.0.3", {"start": v(-26, 56.53) * mm, "end": v(-24, 56.53) * mm});
            skLineSegment(sketch, "E60.15.0.0", {"start": v(-22, 191.53) * mm, "end": v(-22, 56.53) * mm});
            skLineSegment(sketch, "E60.15.0.1", {"start": v(-22, 191.53) * mm, "end": v(-20, 191.53) * mm});
            skLineSegment(sketch, "E60.15.0.2", {"start": v(-20, 191.53) * mm, "end": v(-20, 56.53) * mm});
            skLineSegment(sketch, "E60.15.0.3", {"start": v(-22, 56.53) * mm, "end": v(-20, 56.53) * mm});
            skLineSegment(sketch, "E60.16.0.0", {"start": v(-18, 191.53) * mm, "end": v(-18, 56.53) * mm});
            skLineSegment(sketch, "E60.16.0.1", {"start": v(-18, 191.53) * mm, "end": v(-16, 191.53) * mm});
            skLineSegment(sketch, "E60.16.0.2", {"start": v(-16, 191.53) * mm, "end": v(-16, 56.53) * mm});
            skLineSegment(sketch, "E60.16.0.3", {"start": v(-18, 56.53) * mm, "end": v(-16, 56.53) * mm});
            skLineSegment(sketch, "E60.17.0.0", {"start": v(-14, 191.53) * mm, "end": v(-14, 56.53) * mm});
            skLineSegment(sketch, "E60.17.0.1", {"start": v(-14, 191.53) * mm, "end": v(-12, 191.53) * mm});
            skLineSegment(sketch, "E60.17.0.2", {"start": v(-12, 191.53) * mm, "end": v(-12, 56.53) * mm});
            skLineSegment(sketch, "E60.17.0.3", {"start": v(-14, 56.53) * mm, "end": v(-12, 56.53) * mm});
            skLineSegment(sketch, "E60.18.0.0", {"start": v(-10, 191.53) * mm, "end": v(-10, 56.53) * mm});
            skLineSegment(sketch, "E60.18.0.1", {"start": v(-10, 191.53) * mm, "end": v(-8, 191.53) * mm});
            skLineSegment(sketch, "E60.18.0.2", {"start": v(-8, 191.53) * mm, "end": v(-8, 56.53) * mm});
            skLineSegment(sketch, "E60.18.0.3", {"start": v(-10, 56.53) * mm, "end": v(-8, 56.53) * mm});
            skLineSegment(sketch, "E60.19.0.0", {"start": v(-6, 191.53) * mm, "end": v(-6, 56.53) * mm});
            skLineSegment(sketch, "E60.19.0.1", {"start": v(-6, 191.53) * mm, "end": v(-4, 191.53) * mm});
            skLineSegment(sketch, "E60.19.0.2", {"start": v(-4, 191.53) * mm, "end": v(-4, 56.53) * mm});
            skLineSegment(sketch, "E60.19.0.3", {"start": v(-6, 56.53) * mm, "end": v(-4, 56.53) * mm});
            skLineSegment(sketch, "E60.20.0.0", {"start": v(-2, 191.53) * mm, "end": v(-2, 56.53) * mm});
            skLineSegment(sketch, "E60.20.0.1", {"start": v(-2, 191.53) * mm, "end": v(0, 191.53) * mm});
            skLineSegment(sketch, "E60.20.0.2", {"start": v(0, 191.53) * mm, "end": v(0, 56.53) * mm});
            skLineSegment(sketch, "E60.20.0.3", {"start": v(-2, 56.53) * mm, "end": v(0, 56.53) * mm});
            skLineSegment(sketch, "E60.21.0.0", {"start": v(2, 191.53) * mm, "end": v(2, 56.53) * mm});
            skLineSegment(sketch, "E60.21.0.1", {"start": v(2, 191.53) * mm, "end": v(4, 191.53) * mm});
            skLineSegment(sketch, "E60.21.0.2", {"start": v(4, 191.53) * mm, "end": v(4, 56.53) * mm});
            skLineSegment(sketch, "E60.21.0.3", {"start": v(2, 56.53) * mm, "end": v(4, 56.53) * mm});
            skLineSegment(sketch, "E60.22.0.0", {"start": v(6, 191.53) * mm, "end": v(6, 56.53) * mm});
            skLineSegment(sketch, "E60.22.0.1", {"start": v(6, 191.53) * mm, "end": v(8, 191.53) * mm});
            skLineSegment(sketch, "E60.22.0.2", {"start": v(8, 191.53) * mm, "end": v(8, 56.53) * mm});
            skLineSegment(sketch, "E60.22.0.3", {"start": v(6, 56.53) * mm, "end": v(8, 56.53) * mm});
            skLineSegment(sketch, "E60.direction1", {"start": v(-82, 56.53) * mm, "end": v(-78, 56.53) * mm, "construction": true});
            skSolve(sketch);
        }
        {
            var Q0;
            Q0 = qSketchRegion(id + "F20", true);
            extrude(context, id + "F21", {"entities" : qUnion([Q0]), "operationType" : NewBodyOperationType.ADD, "depth" : 22 * mm});
        }
    });
